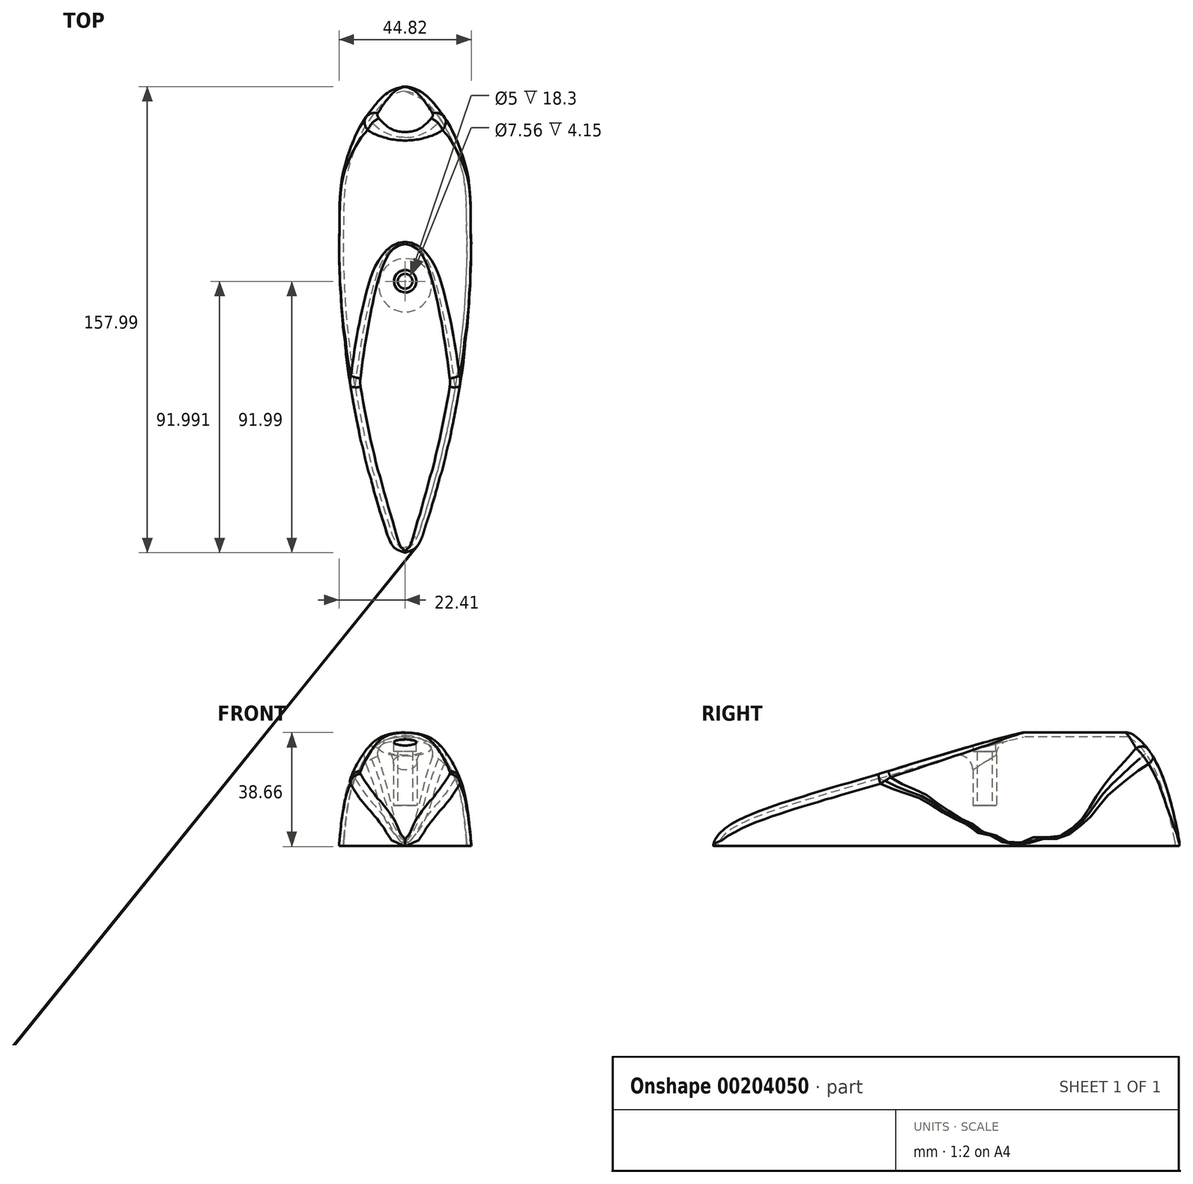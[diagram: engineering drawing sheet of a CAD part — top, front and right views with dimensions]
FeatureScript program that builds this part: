
annotation { "Feature Type Name" : "Feature", "Feature Type Description" : "" }
export const myFeature = defineFeature(function(context is Context, id is Id, definition is map)
    precondition{}
    {
        {
            var Q0;
            Q0=qCreatedBy(makeId("Top.planeOp"),FACE);
            cPlane(context, id + "F0", {"entities" : qUnion([Q0]), "cplaneType" : CPlaneType.OFFSET, "offset" : 47 * mm, "width" : 150 * mm, "height" : 150 * mm});
        }
        {
            var Q0;
            Q0=qCreatedBy(makeId("Top.planeOp"),FACE);
            var sketch = newSketch(context, id + "F1", { "sketchPlane" : qUnion([Q0])});
            skLineSegment(sketch, "E0", {"start": v(0, -79) * mm, "end": v(0, 79) * mm});
            skLineSegment(sketch, "E1", {"start": v(0, 33) * mm, "end": v(22.24, 33) * mm, "construction": true});
            skLineSegment(sketch, "E2.MirrorCS", {"start": v(0, 33) * mm, "end": v(-22.24, 33) * mm, "construction": true});
            skFitSpline(sketch, "E3", {"points": [v(0, 79) * mm, v(-0.6, 78.98) * mm, v(-1.5, 78.8) * mm, v(-4.23, 77.87) * mm, v(-6.65, 76.4) * mm, v(-8.63, 74.56) * mm, v(-10.56, 72.3) * mm, v(-11.48, 71.14) * mm, v(-13.81, 67.88) * mm, v(-15, 65.94) * mm, v(-16.08, 63.86) * mm, v(-17.45, 60.9) * mm, v(-18.83, 57.36) * mm, v(-20.1, 53.47) * mm, v(-20.97, 50.13) * mm, v(-21.5, 47.3) * mm, v(-21.91, 43.43) * mm, v(-22.18, 39.3) * mm, v(-22.24, 35) * mm, v(-22.24, 33) * mm, v(-22.24, 29.88) * mm, v(-22.4, 27.01) * mm, v(-22.4, 23.98) * mm, v(-22.4, 21.1) * mm, v(-22.24, 17.6) * mm, v(-22.1, 14.57) * mm, v(-22.05, 11.5) * mm, v(-21.77, 8.2) * mm, v(-21.64, 5.17) * mm, v(-21.33, 1.37) * mm, v(-21.03, -2.57) * mm, v(-20.57, -5.76) * mm, v(-20.27, -8.8) * mm, v(-19.97, -12.13) * mm, v(-19.51, -16.38) * mm, v(-18.9, -20.02) * mm, v(-18.45, -23.05) * mm, v(-18, -25.63) * mm, v(-17.39, -29.12) * mm, v(-16.93, -31.4) * mm, v(-16.48, -33.82) * mm, v(-15.72, -37.46) * mm, v(-15.11, -40.8) * mm, v(-14.35, -43.38) * mm, v(-13.75, -46.26) * mm, v(-12.99, -49.45) * mm, v(-12.38, -51.72) * mm, v(-11.77, -53.4) * mm, v(-11.17, -55.67) * mm, v(-10.71, -57.49) * mm, v(-10.1, -59.6) * mm, v(-9.2, -62.64) * mm, v(-8.59, -64.92) * mm, v(-7.68, -67.65) * mm, v(-6.92, -69.93) * mm, v(-5.86, -73.41) * mm, v(-4.65, -76) * mm, v(-2.98, -77.81) * mm, v(0, -79) * mm], "startDerivative": vector(-123.77, -1.04) * mm, "endDerivative": vector(67.1, -29.12) * mm});
            skFitSpline(sketch, "E4.MirrorCS", {"points": [v(0, 79) * mm, v(0.6, 78.98) * mm, v(1.5, 78.8) * mm, v(4.23, 77.87) * mm, v(6.65, 76.4) * mm, v(8.63, 74.56) * mm, v(10.56, 72.3) * mm, v(11.48, 71.14) * mm, v(13.81, 67.88) * mm, v(15, 65.94) * mm, v(16.08, 63.86) * mm, v(17.45, 60.9) * mm, v(18.83, 57.36) * mm, v(20.1, 53.47) * mm, v(20.97, 50.13) * mm, v(21.5, 47.3) * mm, v(21.91, 43.43) * mm, v(22.18, 39.3) * mm, v(22.24, 35) * mm, v(22.24, 33) * mm, v(22.24, 29.88) * mm, v(22.4, 27.01) * mm, v(22.4, 23.98) * mm, v(22.4, 21.1) * mm, v(22.24, 17.6) * mm, v(22.1, 14.57) * mm, v(22.05, 11.5) * mm, v(21.77, 8.2) * mm, v(21.64, 5.17) * mm, v(21.33, 1.37) * mm, v(21.03, -2.57) * mm, v(20.57, -5.76) * mm, v(20.27, -8.8) * mm, v(19.97, -12.13) * mm, v(19.51, -16.38) * mm, v(18.9, -20.02) * mm, v(18.45, -23.05) * mm, v(18, -25.63) * mm, v(17.39, -29.12) * mm, v(16.93, -31.4) * mm, v(16.48, -33.82) * mm, v(15.72, -37.46) * mm, v(15.11, -40.8) * mm, v(14.35, -43.38) * mm, v(13.75, -46.26) * mm, v(12.99, -49.45) * mm, v(12.38, -51.72) * mm, v(11.77, -53.4) * mm, v(11.17, -55.67) * mm, v(10.71, -57.49) * mm, v(10.1, -59.6) * mm, v(9.2, -62.64) * mm, v(8.59, -64.92) * mm, v(7.68, -67.65) * mm, v(6.92, -69.93) * mm, v(5.86, -73.41) * mm, v(4.65, -76) * mm, v(2.98, -77.81) * mm, v(0, -79) * mm], "startDerivative": vector(123.77, -1.04) * mm, "endDerivative": vector(-67.1, -29.12) * mm});
            skCircle(sketch, "E5", {"center": v(0, 13) * mm, "radius": 2.5 * mm});
            skSolve(sketch);
        }
        {
            var Q0;
            Q0=qCreatedBy(makeId("Right.planeOp"),FACE);
            var sketch = newSketch(context, id + "F2", { "sketchPlane" : qUnion([Q0])});
            skFitSpline(sketch, "E6", {"points": [v(-79.5, 0) * mm, v(-75.78, 5.39) * mm, v(-59.62, 13.19) * mm, v(-16.42, 26.36) * mm, v(46.42, 41.57) * mm, v(67.6, 33.8) * mm, v(79.3, 0) * mm], "startDerivative": vector(35.31, 69.6) * mm, "endDerivative": vector(40.62, -222.13) * mm});
            skLineSegment(sketch, "E7", {"start": v(79.3, 0) * mm, "end": v(-79.5, 0) * mm});
            skLineSegment(sketch, "E8", {"start": v(79.3, 0) * mm, "end": v(113.67, 0) * mm});
            skLineSegment(sketch, "E9", {"start": v(113.67, 0) * mm, "end": v(113.67, 67.8) * mm});
            skLineSegment(sketch, "E10", {"start": v(113.67, 67.8) * mm, "end": v(-79.5, 67.8) * mm});
            skLineSegment(sketch, "E11", {"start": v(-79.5, 67.8) * mm, "end": v(-79.5, 0) * mm});
            skSolve(sketch);
        }
        {
            var Q0;
            Q0=qCreatedBy(makeId("Front.planeOp"),FACE);
            var sketch = newSketch(context, id + "F3", { "sketchPlane" : qUnion([Q0])});
            skFitSpline(sketch, "E12", {"points": [v(-22.47, 0) * mm, v(-20.24, 17.27) * mm, v(-17.27, 25.82) * mm, v(-12.63, 33.25) * mm, v(0, 38.45) * mm], "startDerivative": vector(5.53, 62.71) * mm, "endDerivative": vector(78.66, 0) * mm});
            skLineSegment(sketch, "E13", {"start": v(0, 0) * mm, "end": v(0, 56.83) * mm, "construction": true});
            skFitSpline(sketch, "E14.MirrorCS", {"points": [v(22.47, 0) * mm, v(20.24, 17.27) * mm, v(17.27, 25.82) * mm, v(12.63, 33.25) * mm, v(0, 38.45) * mm], "startDerivative": vector(-5.53, 62.71) * mm, "endDerivative": vector(-78.66, 0) * mm});
            skLineSegment(sketch, "E15", {"start": v(-22.47, 0) * mm, "end": v(22.47, 0) * mm});
            skLineSegment(sketch, "E16", {"start": v(-22.47, 0) * mm, "end": v(-34.17, 0) * mm});
            skLineSegment(sketch, "E17", {"start": v(-34.17, 0) * mm, "end": v(-34.17, 51.82) * mm});
            skLineSegment(sketch, "E18", {"start": v(-34.17, 51.82) * mm, "end": v(33.25, 51.82) * mm});
            skLineSegment(sketch, "E19", {"start": v(33.25, 51.82) * mm, "end": v(33.25, 0) * mm});
            skLineSegment(sketch, "E20", {"start": v(33.25, 0) * mm, "end": v(22.47, 0) * mm});
            skSolve(sketch);
        }
        {
            var Q0;
            Q0=qCreatedBy(makeId("Top.planeOp"),FACE);
            var sketch = newSketch(context, id + "F4", { "sketchPlane" : qUnion([Q0])});
            skCircle(sketch, "E21", {"center": v(0, 12.98) * mm, "radius": 9.8 * mm});
            skSolve(sketch);
        }
        {
            var Q0;
            Q0=qCreatedBy(id+"F0.planeOp",FACE);
            var sketch = newSketch(context, id + "F5", { "sketchPlane" : qUnion([Q0])});
            skCircle(sketch, "E22", {"center": v(0, 13) * mm, "radius": 3.78 * mm});
            skSolve(sketch);
        }
        {
            var Q0;
            {var subQ0=sQuery(id+"F1.wireOp",EDGE,"E4.MirrorCS");Q0=makeQuery(id+"F1.imprint","IMPRINT",FACE,{"disambiguationData":[TD([[makeQuery(id+"F1.imprint","IMPRINT",EDGE,{"derivedFrom":subQ0}),-1.0]])]});}
            var Q1;
            {var subQ1=sQuery(id+"F1.wireOp",EDGE,"E3");Q1=makeQuery(id+"F1.imprint","IMPRINT",FACE,{"disambiguationData":[TD([[makeQuery(id+"F1.imprint","IMPRINT",EDGE,{"derivedFrom":subQ1}),1.0]])]});}
            extrude(context, id + "F6", {"entities" : qUnion([Q0, Q1]), "depth" : 47.8 * mm, "offsetDistance" : 25 * mm});
        }
        {
            var Q0;
            Q0=makeQuery(id+"F2.imprint","IMPRINT",FACE,{"disambiguationData":[TD([[makeQuery(id+"F2.imprint","IMPRINT",EDGE,{"derivedFrom":sQuery(id+"F2.wireOp",EDGE,"E6")}),1.0]])]});
            extrude(context, id + "F7", {"entities" : qUnion([Q0]), "operationType" : NewBodyOperationType.REMOVE, "endBound" : BoundingType.SYMMETRIC, "depth" : 58.6 * mm, "offsetDistance" : 25 * mm});
        }
        {
            var Q0;
            Q0=makeQuery(id+"F3.imprint","IMPRINT",FACE,{"disambiguationData":[TD([[makeQuery(id+"F3.imprint","IMPRINT",EDGE,{"derivedFrom":sQuery(id+"F3.wireOp",EDGE,"E12")}),1.0]])]});
            extrude(context, id + "F8", {"entities" : qUnion([Q0]), "operationType" : NewBodyOperationType.REMOVE, "endBound" : BoundingType.SYMMETRIC, "oppositeDirection" : true, "depth" : 166 * mm, "offsetDistance" : 25 * mm});
        }
        {
            var Q0;
            Q0=makeQuery(id+"F6.opExtrude","CAP_FACE",FACE,{"disambiguationData":[OSD([sQuery(id+"F1.wireOp",EDGE,"E3"),sQuery(id+"F1.wireOp",EDGE,"E4.MirrorCS"),sQuery(id+"F1.wireOp",EDGE,"E5")])],"isStart":true});
            shell(context, id + "F9", {"entities" : qUnion([Q0]), "thickness" : 1.5 * mm});
        }
        {
            var Q0;
            Q0=makeQuery(id+"F8.boolean.opBoolean","SPLIT",EDGE,{"disambiguationData":[OD(1.0)],"derivedFrom":makeQuery(id+"F7.boolean.opBoolean","INTERSECT",EDGE,{"derivedFrom":[makeQuery(id+"F6.opExtrude","SWEPT_FACE",FACE,{"disambiguationData":[OSD([sQuery(id+"F1.wireOp",EDGE,"E3")])]}),makeQuery(id+"F7.opExtrude","SWEPT_FACE",FACE,{"disambiguationData":[OSD([sQuery(id+"F2.wireOp",EDGE,"E6")])]})]})});
            var Q1;
            Q1=makeQuery(id+"F8.boolean.opBoolean","INTERSECT",EDGE,{"disambiguationData":[OD(0.0)],"derivedFrom":[makeQuery(id+"F7.boolean.opBoolean","COPY",FACE,{"derivedFrom":makeQuery(id+"F7.opExtrude","SWEPT_FACE",FACE,{"disambiguationData":[OSD([sQuery(id+"F2.wireOp",EDGE,"E6")])]})}),makeQuery(id+"F8.opExtrude","SWEPT_FACE",FACE,{"disambiguationData":[OSD([sQuery(id+"F3.wireOp",EDGE,"E12")])]})]});
            var Q2;
            Q2=makeQuery(id+"F8.boolean.opBoolean","SPLIT",EDGE,{"disambiguationData":[OD(1.0)],"derivedFrom":makeQuery(id+"F7.boolean.opBoolean","INTERSECT",EDGE,{"derivedFrom":[makeQuery(id+"F6.opExtrude","SWEPT_FACE",FACE,{"disambiguationData":[OSD([sQuery(id+"F1.wireOp",EDGE,"E4.MirrorCS")])]}),makeQuery(id+"F7.opExtrude","SWEPT_FACE",FACE,{"disambiguationData":[OSD([sQuery(id+"F2.wireOp",EDGE,"E6")])]})]})});
            fillet(context, id + "F10", {"entities" : qUnion([Q0, Q1, Q2]), "radius" : 5 * mm, "tangentPropagation" : true, "allowEdgeOverflow" : false});
        }
        {
            var Q0;
            Q0=makeQuery(id+"F8.boolean.opBoolean","INTERSECT",EDGE,{"derivedFrom":[makeQuery(id+"F6.opExtrude","SWEPT_FACE",FACE,{"disambiguationData":[OSD([sQuery(id+"F1.wireOp",EDGE,"E4.MirrorCS")])]}),makeQuery(id+"F8.opExtrude","SWEPT_FACE",FACE,{"disambiguationData":[OSD([sQuery(id+"F3.wireOp",EDGE,"E14.MirrorCS")])]})]});
            var Q1;
            Q1=makeQuery(id+"F8.boolean.opBoolean","INTERSECT",EDGE,{"derivedFrom":[makeQuery(id+"F6.opExtrude","SWEPT_FACE",FACE,{"disambiguationData":[OSD([sQuery(id+"F1.wireOp",EDGE,"E3")])]}),makeQuery(id+"F8.opExtrude","SWEPT_FACE",FACE,{"disambiguationData":[OSD([sQuery(id+"F3.wireOp",EDGE,"E12")])]})]});
            fillet(context, id + "F11", {"entities" : qUnion([Q0, Q1]), "radius" : 8 * mm, "tangentPropagation" : true, "allowEdgeOverflow" : false});
        }
        {
            var Q0;
            Q0=makeQuery(id+"F8.boolean.opBoolean","INTERSECT",EDGE,{"disambiguationData":[OD(1.0)],"derivedFrom":[makeQuery(id+"F7.boolean.opBoolean","COPY",FACE,{"derivedFrom":makeQuery(id+"F7.opExtrude","SWEPT_FACE",FACE,{"disambiguationData":[OSD([sQuery(id+"F2.wireOp",EDGE,"E6")])]})}),makeQuery(id+"F8.opExtrude","SWEPT_FACE",FACE,{"disambiguationData":[OSD([sQuery(id+"F3.wireOp",EDGE,"E14.MirrorCS")])]})]});
            var Q1;
            Q1=makeQuery(id+"F8.boolean.opBoolean","INTERSECT",EDGE,{"disambiguationData":[OD(1.0)],"derivedFrom":[makeQuery(id+"F7.boolean.opBoolean","COPY",FACE,{"derivedFrom":makeQuery(id+"F7.opExtrude","SWEPT_FACE",FACE,{"disambiguationData":[OSD([sQuery(id+"F2.wireOp",EDGE,"E6")])]})}),makeQuery(id+"F8.opExtrude","SWEPT_FACE",FACE,{"disambiguationData":[OSD([sQuery(id+"F3.wireOp",EDGE,"E12")])]})]});
            fillet(context, id + "F12", {"entities" : qUnion([Q0, Q1]), "radius" : 3.5 * mm, "tangentPropagation" : true, "allowEdgeOverflow" : false});
        }
        {
            var Q0;
            Q0=makeQuery(id+"F9.opShell","OFFSET_EDGE",EDGE,{"disambiguationData":[OSD([sQuery(id+"F1.wireOp",EDGE,"E5"),sQuery(id+"F2.wireOp",EDGE,"E6")])]});
            fillet(context, id + "F13", {"entities" : qUnion([Q0]), "radius" : 5 * mm, "tangentPropagation" : true, "allowEdgeOverflow" : false});
        }
        {
            var Q0;
            Q0=makeQuery(id+"F4.imprint","IMPRINT",FACE,{"disambiguationData":[TD([[makeQuery(id+"F4.imprint","IMPRINT",EDGE,{"derivedFrom":sQuery(id+"F4.wireOp",EDGE,"E21")}),1.0]])]});
            extrude(context, id + "F14", {"entities" : qUnion([Q0]), "operationType" : NewBodyOperationType.REMOVE, "depth" : 13.7 * mm, "offsetDistance" : 25 * mm});
        }
        {
            var Q0;
            Q0 = qSketchRegion(id + "F5", true);
            extrude(context, id + "F15", {"entities" : qUnion([Q0]), "operationType" : NewBodyOperationType.REMOVE, "oppositeDirection" : true, "depth" : 15 * mm, "offsetDistance" : 25 * mm});
        }
    });
